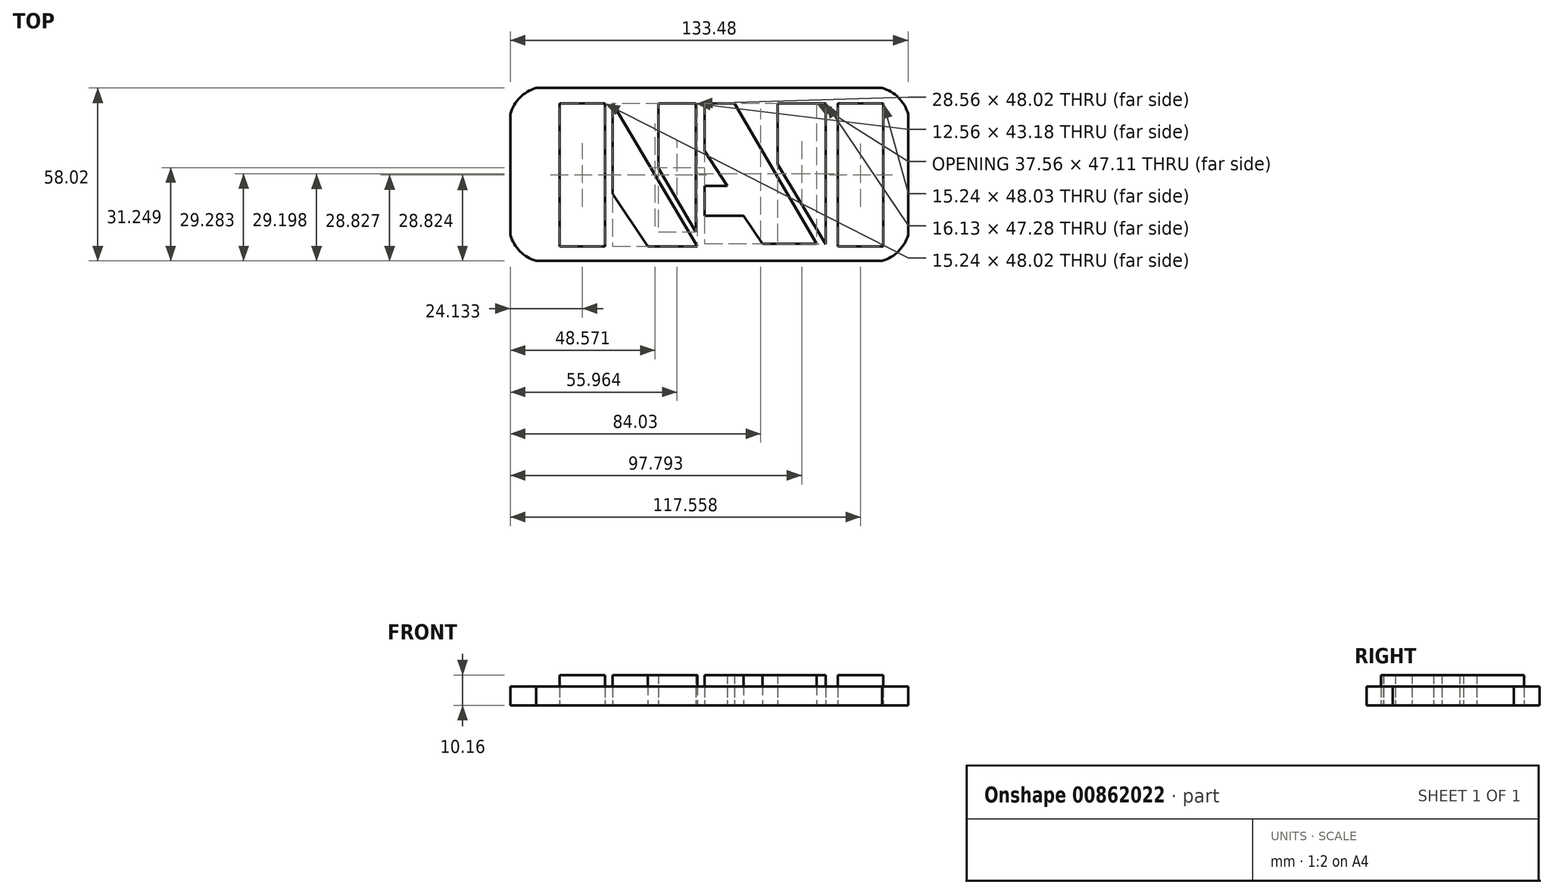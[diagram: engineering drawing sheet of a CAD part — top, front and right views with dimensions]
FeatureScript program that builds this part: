
annotation { "Feature Type Name" : "Feature", "Feature Type Description" : "" }
export const myFeature = defineFeature(function(context is Context, id is Id, definition is map)
    precondition{}
    {
        {
            var Q0;
            Q0=qCreatedBy(makeId("Top.planeOp"),FACE);
            var sketch = newSketch(context, id + "F0", { "sketchPlane" : qUnion([Q0])});
            skLineSegment(sketch, "E0.bottom", {"start": v(-59.22, 35.6) * mm, "end": v(56.83, 35.6) * mm});
            skLineSegment(sketch, "E0.top", {"start": v(-59.22, -22.43) * mm, "end": v(56.83, -22.43) * mm});
            skLineSegment(sketch, "E0.left", {"start": v(-67.94, 26.88) * mm, "end": v(-67.94, -13.72) * mm});
            skLineSegment(sketch, "E0.right", {"start": v(65.54, 26.88) * mm, "end": v(65.54, -13.72) * mm});
            skArc(sketch, "E1", {"start": v(-59.22, 35.6) * mm, "mid": v(-64.7, 32.36) * mm, "end": v(-67.94, 26.88) * mm});
            skArc(sketch, "E2", {"start": v(65.54, 26.88) * mm, "mid": v(62.32, 32.36) * mm, "end": v(56.83, 35.6) * mm});
            skArc(sketch, "E3", {"start": v(-67.94, -13.72) * mm, "mid": v(-64.7, -19.2) * mm, "end": v(-59.22, -22.43) * mm});
            skArc(sketch, "E4", {"start": v(56.83, -22.43) * mm, "mid": v(62.32, -19.2) * mm, "end": v(65.54, -13.72) * mm});
            skPoint(sketch, "E5.orphan", {"position": v(-67.94, -22.43) * mm});
            skPoint(sketch, "E6.orphan", {"position": v(-67.94, 35.6) * mm});
            skPoint(sketch, "E7.orphan", {"position": v(65.54, 35.6) * mm});
            skPoint(sketch, "E8.orphan", {"position": v(65.54, -22.43) * mm});
            skLineSegment(sketch, "E9.bottom", {"start": v(-51.43, 30.4) * mm, "end": v(-36.19, 30.4) * mm});
            skLineSegment(sketch, "E9.top", {"start": v(-51.43, -17.62) * mm, "end": v(-36.19, -17.62) * mm});
            skLineSegment(sketch, "E9.left", {"start": v(-51.43, 30.4) * mm, "end": v(-51.43, -17.62) * mm});
            skLineSegment(sketch, "E9.right", {"start": v(-36.19, 30.4) * mm, "end": v(-36.19, -17.62) * mm});
            skLineSegment(sketch, "E10.bottom", {"start": v(-21.78, -17.62) * mm, "end": v(-5.1, -17.62) * mm});
            skLineSegment(sketch, "E10.left", {"start": v(-33.65, 0) * mm, "end": v(-33.65, 30.4) * mm});
            skLineSegment(sketch, "E11", {"start": v(-33.65, 30.4) * mm, "end": v(-5.1, -17.62) * mm});
            skLineSegment(sketch, "E12", {"start": v(-33.65, 0) * mm, "end": v(-21.78, -17.62) * mm});
            skPoint(sketch, "E13.orphan", {"position": v(-33.65, -17.62) * mm});
            skLineSegment(sketch, "E14", {"start": v(-18.26, 30.4) * mm, "end": v(-5.7, 30.4) * mm});
            skLineSegment(sketch, "E15", {"start": v(-5.7, 30.4) * mm, "end": v(-5.7, -12.77) * mm});
            skLineSegment(sketch, "E16", {"start": v(-18.26, 30.4) * mm, "end": v(-18.26, 8.71) * mm});
            skLineSegment(sketch, "E17", {"start": v(-18.26, 8.71) * mm, "end": v(-5.7, -12.77) * mm});
            skLineSegment(sketch, "E18.bottom", {"start": v(-2.69, 30.4) * mm, "end": v(7.32, 30.4) * mm});
            skLineSegment(sketch, "E18.left", {"start": v(-2.69, 30.4) * mm, "end": v(-2.69, 14.46) * mm});
            skPoint(sketch, "E19", {"position": v(-2.69, 14.46) * mm});
            skLineSegment(sketch, "E20", {"start": v(-2.69, 14.46) * mm, "end": v(4.91, 2.78) * mm});
            skLineSegment(sketch, "E21", {"start": v(4.91, 2.78) * mm, "end": v(-2.69, 2.78) * mm});
            skPoint(sketch, "E22", {"position": v(-2.69, -7.25) * mm});
            skLineSegment(sketch, "E23", {"start": v(-2.69, -7.25) * mm, "end": v(10.4, -7.25) * mm});
            skLineSegment(sketch, "E24", {"start": v(10.4, -7.25) * mm, "end": v(16.7, -16.7) * mm});
            skLineSegment(sketch, "E25", {"start": v(7.32, 30.4) * mm, "end": v(34.87, -16.7) * mm});
            skLineSegment(sketch, "E26", {"start": v(34.87, -16.7) * mm, "end": v(16.7, -16.7) * mm});
            skLineSegment(sketch, "E27.trimOffspring", {"start": v(-2.69, 2.78) * mm, "end": v(-2.69, -7.25) * mm});
            skLineSegment(sketch, "E28.left", {"start": v(21.79, 30.4) * mm, "end": v(21.79, 10.01) * mm});
            skPoint(sketch, "E29", {"position": v(21.79, 10.01) * mm});
            skLineSegment(sketch, "E30", {"start": v(21.79, 10.01) * mm, "end": v(37.92, -16.87) * mm});
            skLineSegment(sketch, "E31", {"start": v(37.92, -16.87) * mm, "end": v(37.92, 30.4) * mm});
            skLineSegment(sketch, "E32", {"start": v(37.92, 30.4) * mm, "end": v(21.79, 30.4) * mm});
            skLineSegment(sketch, "E33.bottom", {"start": v(42, 30.4) * mm, "end": v(57.24, 30.4) * mm});
            skLineSegment(sketch, "E33.top", {"start": v(42, -17.62) * mm, "end": v(57.24, -17.62) * mm});
            skLineSegment(sketch, "E33.left", {"start": v(42, 30.4) * mm, "end": v(42, -17.62) * mm});
            skLineSegment(sketch, "E33.right", {"start": v(57.24, 30.4) * mm, "end": v(57.24, -17.62) * mm});
            skSolve(sketch);
        }
        {
            var Q0;
            Q0=makeQuery(id+"F0.imprint","IMPRINT",FACE,{"disambiguationData":[TD([[makeQuery(id+"F0.imprint","IMPRINT",EDGE,{"derivedFrom":sQuery(id+"F0.wireOp",EDGE,"E9.bottom")}),-1.0]])]});
            var Q1;
            Q1=makeQuery(id+"F0.imprint","IMPRINT",FACE,{"disambiguationData":[TD([[makeQuery(id+"F0.imprint","IMPRINT",EDGE,{"derivedFrom":sQuery(id+"F0.wireOp",EDGE,"E10.bottom")}),1.0]])]});
            var Q2;
            Q2=makeQuery(id+"F0.imprint","IMPRINT",FACE,{"disambiguationData":[TD([[makeQuery(id+"F0.imprint","IMPRINT",EDGE,{"derivedFrom":sQuery(id+"F0.wireOp",EDGE,"E14")}),-1.0]])]});
            var Q3;
            Q3=makeQuery(id+"F0.imprint","IMPRINT",FACE,{"disambiguationData":[TD([[makeQuery(id+"F0.imprint","IMPRINT",EDGE,{"derivedFrom":sQuery(id+"F0.wireOp",EDGE,"E18.left")}),1.0]])]});
            var Q4;
            Q4=makeQuery(id+"F0.imprint","IMPRINT",FACE,{"disambiguationData":[TD([[makeQuery(id+"F0.imprint","IMPRINT",EDGE,{"derivedFrom":sQuery(id+"F0.wireOp",EDGE,"E28.left")}),1.0]])]});
            var Q5;
            Q5=makeQuery(id+"F0.imprint","IMPRINT",FACE,{"disambiguationData":[TD([[makeQuery(id+"F0.imprint","IMPRINT",EDGE,{"derivedFrom":sQuery(id+"F0.wireOp",EDGE,"E33.bottom")}),-1.0]])]});
            extrude(context, id + "F1", {"entities" : qUnion([Q0, Q1, Q2, Q3, Q4, Q5]), "depth" : 10.16 * mm, "offsetDistance" : 25.4 * mm});
        }
        {
            var Q0;
            Q0=makeQuery(id+"F0.imprint","IMPRINT",FACE,{"disambiguationData":[TD([[makeQuery(id+"F0.imprint","IMPRINT",EDGE,{"derivedFrom":sQuery(id+"F0.wireOp",EDGE,"E0.bottom")}),-1.0]])]});
            extrude(context, id + "F2", {"entities" : qUnion([Q0]), "depth" : 6.35 * mm, "offsetDistance" : 25.4 * mm});
        }
    });
